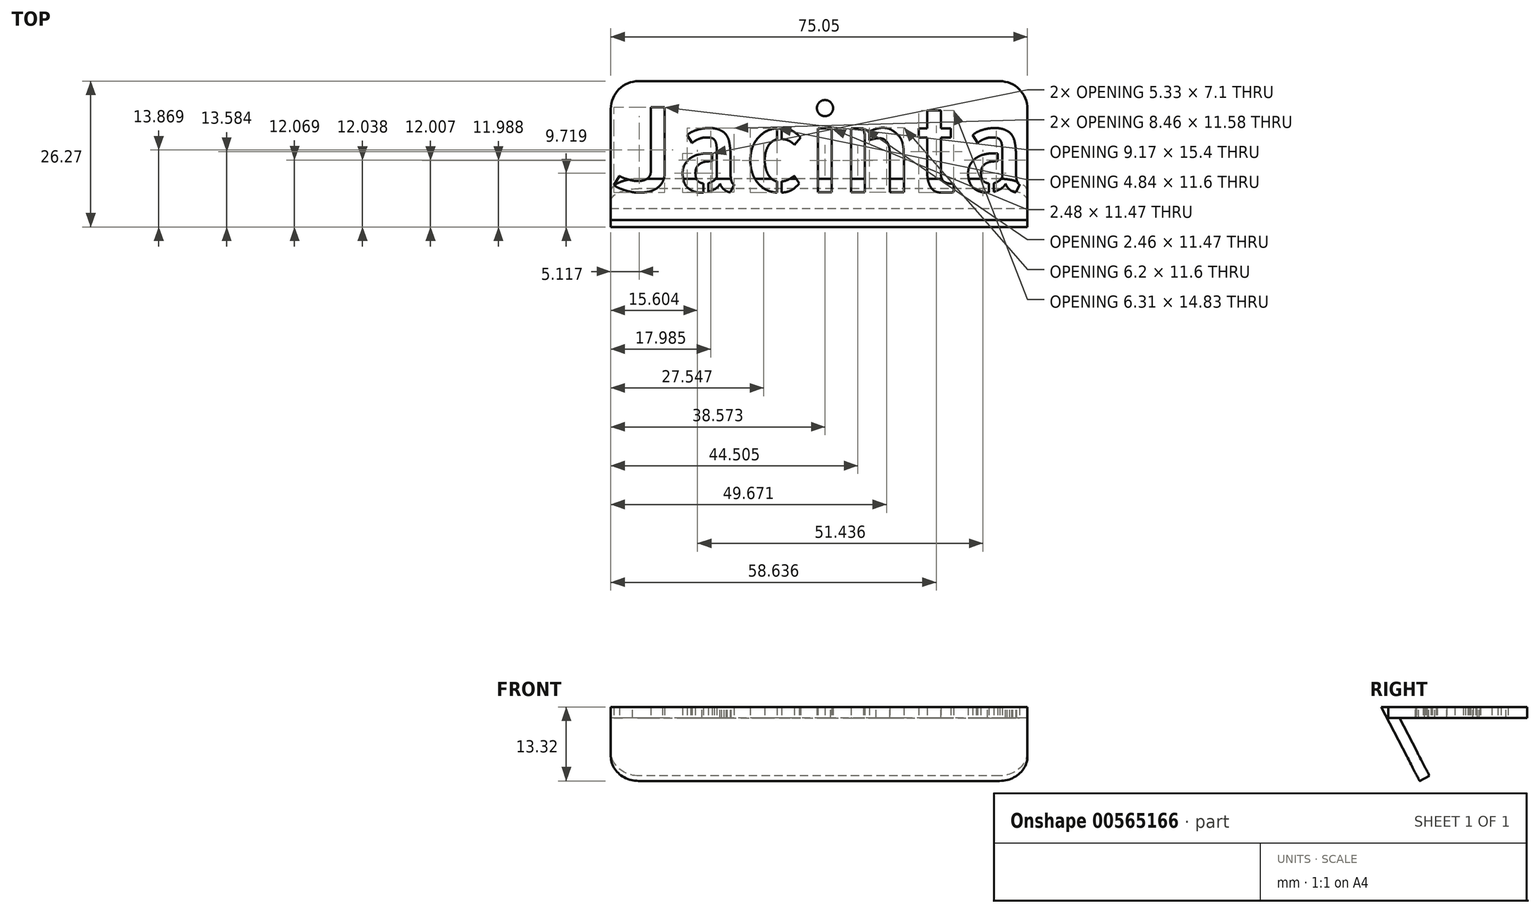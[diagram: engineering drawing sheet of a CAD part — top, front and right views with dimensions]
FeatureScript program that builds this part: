
annotation { "Feature Type Name" : "Feature", "Feature Type Description" : "" }
export const myFeature = defineFeature(function(context is Context, id is Id, definition is map)
    precondition{}
    {
        {
            var Q0;
            Q0=qCreatedBy(makeId("Top.planeOp"),FACE);
            var sketch = newSketch(context, id + "F0", { "sketchPlane" : qUnion([Q0])});
            skLineSegment(sketch, "E0.bottom", {"start": v(-23.58, 12.5) * mm, "end": v(51.47, 12.5) * mm});
            skLineSegment(sketch, "E0.top", {"start": v(-23.58, -12.5) * mm, "end": v(51.47, -12.5) * mm});
            skLineSegment(sketch, "E0.left", {"start": v(-23.58, 12.5) * mm, "end": v(-23.58, -12.5) * mm});
            skLineSegment(sketch, "E0.right", {"start": v(51.47, 12.5) * mm, "end": v(51.47, -12.5) * mm});
            skText(sketch, "E1", { "text": "Jacinta", "fontName": "AllertaStencil-Regular.ttf"});
            const initialGuessF0  = {"E1": [-0.02358, -0.0075, 1, 0, 0.015]};
            skSetInitialGuess(sketch, initialGuessF0);
            skSolve(sketch);
        }
        {
            var Q0;
            Q0=makeQuery(id+"F0.imprint","IMPRINT",FACE,{"disambiguationData":[TD([[makeQuery(id+"F0.imprint","IMPRINT",EDGE,{"derivedFrom":sQuery(id+"F0.wireOp",EDGE,"E0.bottom")}),-1.0]])]});
            extrude(context, id + "F1", {"entities" : qUnion([Q0]), "depth" : 2 * mm, "offsetDistance" : 25 * mm});
        }
        {
            var Q0;
            {var subQ0=sQuery(id+"F0.wireOp",EDGE,"E0.left");Q0=makeQuery(id+"FYEOEdhl7jzHk82_2.opBoolean","MERGE",FACE,{"derivedFrom":[makeQuery(id+"F1.opExtrude","SWEPT_FACE",FACE,{"disambiguationData":[OSD([subQ0])]}),makeQuery(id+"FOv1BJgTRWeWuMw_1.opExtrude","CAP_FACE",FACE,{"disambiguationData":[OSD([sQuery(id+"F0.wireOp",EDGE,"E0.bottom"),subQ0,sQuery(id+"Fjco5yBOxZZxTCI_1.wireOp",EDGE,"TpTMtmOo-qoIM-rLEy-p7IH-mKgsBanMGF23"),sQuery(id+"Fjco5yBOxZZxTCI_1.wireOp",EDGE,"Ja6BvVoQ-cpFi-Lcom-cL8s-5xC4kZiynyNl"),sQuery(id+"Fjco5yBOxZZxTCI_1.wireOp",EDGE,"utNyaJ8P-FD6r-AD7x-tpFW-fHytfVhziHLl"),sQuery(id+"Fjco5yBOxZZxTCI_1.wireOp",EDGE,"xGzW29bi-H5H8-ObLh-gdKj-mSPkAtMAUUzO")])],"isStart":true})]});}
            var sketch = newSketch(context, id + "F2", { "sketchPlane" : qUnion([Q0])});
            skLineSegment(sketch, "E2", {"start": v(11.52, 2) * mm, "end": v(5.09, -10.4) * mm});
            skLineSegment(sketch, "E3", {"start": v(5.09, -10.4) * mm, "end": v(6.87, -11.32) * mm});
            skLineSegment(sketch, "E4", {"start": v(6.87, -11.32) * mm, "end": v(13.77, 2) * mm});
            skLineSegment(sketch, "E5", {"start": v(13.77, 2) * mm, "end": v(11.52, 2) * mm});
            skSolve(sketch);
        }
        {
            var Q0;
            {var subQ4=sQuery(id+"F2.wireOp",EDGE,"E3");Q0=makeQuery(id+"F2.imprint","IMPRINT",FACE,{"disambiguationData":[TD([[makeQuery(id+"F2.imprint","IMPRINT",EDGE,{"derivedFrom":subQ4}),1.0]])]});}
            var Q1;
            Q1=makeQuery(id+"F1.opExtrude","SWEPT_FACE",FACE,{"disambiguationData":[OSD([sQuery(id+"F0.wireOp",EDGE,"E0.right")])]});
            extrude(context, id + "F3", {"entities" : qUnion([Q0]), "endBound" : BoundingType.UP_TO_SURFACE, "oppositeDirection" : true, "depth" : 75 * mm, "endBoundEntityFace" : qUnion([Q1]), "offsetDistance" : 25 * mm});
        }
        {
            var Q0;
            Q0=makeQuery(id+"F1.opExtrude","SWEPT_EDGE",EDGE,{"disambiguationData":[OSD([sQuery(id+"F0.wireOp",EDGE,"E0.bottom"),sQuery(id+"F0.wireOp",EDGE,"E0.left")])]});
            var Q1;
            Q1=makeQuery(id+"F1.opExtrude","SWEPT_EDGE",EDGE,{"disambiguationData":[OSD([sQuery(id+"F0.wireOp",EDGE,"E0.bottom"),sQuery(id+"F0.wireOp",EDGE,"E0.right")])]});
            var Q2;
            Q2=makeQuery(id+"F3.opExtrude","CAP_EDGE",EDGE,{"disambiguationData":[OSD([sQuery(id+"F2.wireOp",EDGE,"E3")])],"isStart":false});
            var Q3;
            Q3=makeQuery(id+"F3.opExtrude","CAP_EDGE",EDGE,{"disambiguationData":[OSD([sQuery(id+"F2.wireOp",EDGE,"E3")])],"isStart":true});
            var Q4;
            Q4=makeQuery(id+"F3.opExtrude","TWEAK_EDGE",EDGE,{"derivedFrom":[makeQuery(id+"F1.opExtrude","SWEPT_FACE",FACE,{"disambiguationData":[OSD([sQuery(id+"F0.wireOp",EDGE,"E0.right")])]}),makeQuery(id+"F2.imprint","IMPRINT",EDGE,{"derivedFrom":sQuery(id+"F2.wireOp",EDGE,"E3")})]});
            fillet(context, id + "F4", {"entities" : qUnion([Q0, Q1, Q2, Q3, Q4]), "radius" : 5 * mm, "tangentPropagation" : true, "allowEdgeOverflow" : false});
        }
    });
